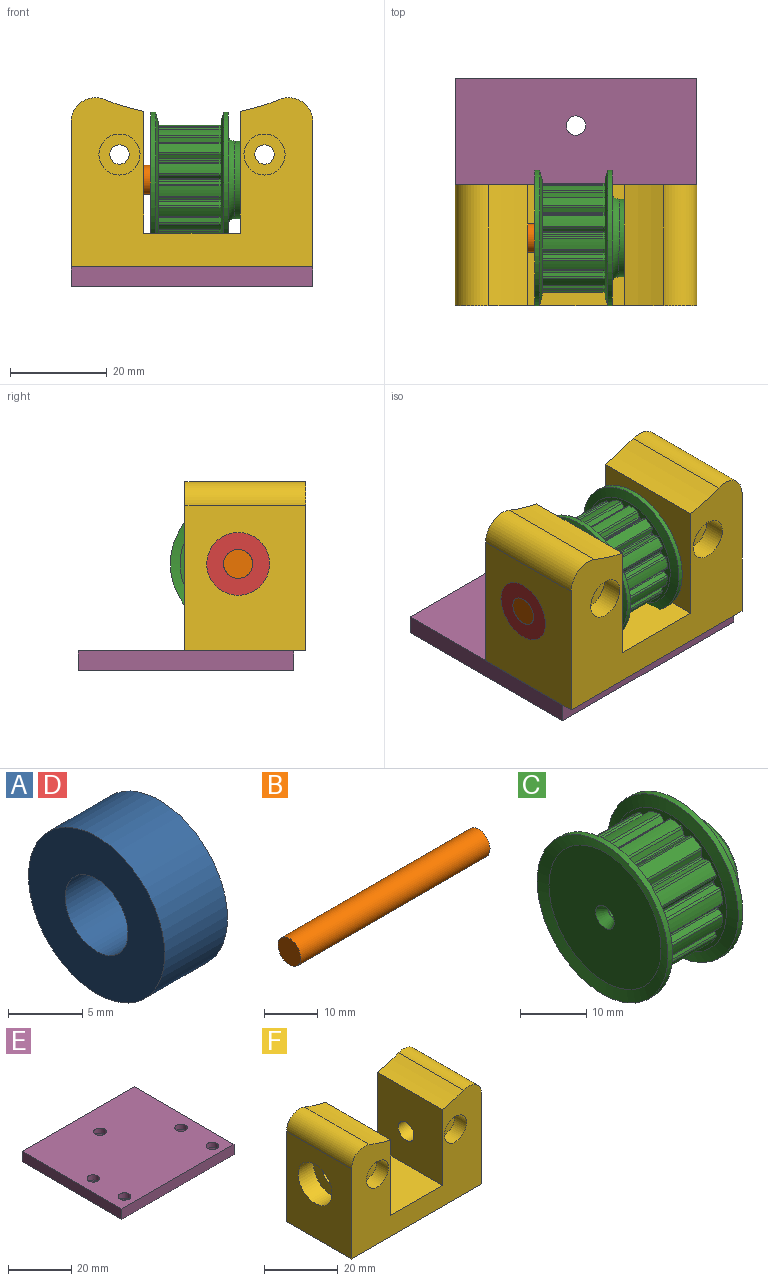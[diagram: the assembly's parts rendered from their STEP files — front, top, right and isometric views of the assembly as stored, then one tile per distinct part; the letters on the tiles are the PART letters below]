
ASSEMBLY  parts=6 mates=5
PART A: 4 faces, bbox 6x13x13 mm
  f0: cylinder r=3mm len=6mm, axis (1,0,0), area 113.1mm2, adj f2,f3
  f1: cylinder r=6.5mm len=13mm, axis (1,0,0), area 245mm2, adj f2,f3
  f2: plane 13x13mm, normal (-1,0,0), area 104.5mm2, adj f0,f1
  f3: plane 13x13mm, normal (1,0,0), area 104.5mm2, adj f0,f1
PART B: 3 faces, bbox 50x6x6 mm
  f0: cylinder r=3mm len=50mm, axis (1,0,0), area 942.5mm2, adj f1,f2
  f1: plane 6x6mm, normal (-1,0,0), area 28.3mm2, adj f0
  f2: plane 6x6mm, normal (1,0,0), area 28.3mm2, adj f0
PART C: 128 faces, bbox 21.5x28x28 mm
  f0: cone r=13mm half-angle=75deg, axis (-1,0,0), area 169.1mm2, adj f1,f27
  f1: cylinder r=14mm len=28mm, axis (1,0,0), area 88mm2, adj f0,f2
  f2: cone r=13mm half-angle=75deg, axis (-1,0,0), area 169.1mm2, adj f1,f126
  f3: cone r=13mm half-angle=75deg, axis (1,0,0), area 169.1mm2, adj f4,f36
  f4: cylinder r=14mm len=28mm, axis (-1,0,0), area 88mm2, adj f3,f5
  f5: cone r=13mm half-angle=75deg, axis (1,0,0), area 169.1mm2, adj f4,f127
  f6: cylinder r=8mm len=16mm, axis (1,0,0), area 179.9mm2, adj f7,f15,f17
  f7: cone r=7.75mm half-angle=45deg, axis (-1,0,0), area 34.4mm2, adj f6,f18
  f8: cone r=0.5mm half-angle=30deg, axis (-1,0,0), area 6.3mm2, adj f9
  f9: cylinder r=1mm len=2mm, axis (1,0,0), area 9.7mm2, adj f8,f10
  f10: cone r=1.5mm half-angle=30deg, axis (-1,0,0), area 18.8mm2, adj f9,f126
  f11: cone r=0.5mm half-angle=30deg, axis (1,0,0), area 4.2mm2, adj f12,f16
  f12: cylinder r=1mm len=2mm, axis (-1,0,0), area 9.7mm2, adj f11,f13
  f13: cone r=1.5mm half-angle=30deg, axis (1,0,0), area 18.8mm2, adj f12,f18
  f14: cylinder r=10mm len=20mm, axis (1,0,0), area 0.1mm2, adj f15,f127
  f15: torus R=10mm, axis (1,0,0), area 168.2mm2, adj f6,f14,f17
  f16: plane 1.15x1.15mm, normal (1,0,0), area 1mm2, adj f11
  f17: plane 15.97x8.73mm, normal (1,0,0), area 0.2mm2, adj f6,f15
  f18: plane 15x15mm, normal (1,0,0), area 164.1mm2, adj f7,f13
  f19: plane 13x0.77mm, normal (0,0.75,0.66), area 13.2mm2, adj f20,f25,f27,f36
  f20: cylinder r=0.6mm len=13mm, axis (1,0,0), area 5.5mm2, adj f19,f21,f27,f36
  f21: cylinder r=11.32mm len=13mm, axis (1,0,0), area 29.2mm2, adj f20,f22,f27,f36
  f22: cylinder r=0.6mm len=13mm, axis (1,0,0), area 5.5mm2, adj f21,f23,f27,f36
  f23: plane 13x1.02mm, normal (0,0.02,-1), area 13.2mm2, adj f22,f24,f27,f36
  f24: cylinder r=0.4mm len=13mm, axis (1,0,0), area 4.4mm2, adj f23,f27,f33,f36
  f25: cylinder r=0.4mm len=13mm, axis (1,0,0), area 4.4mm2, adj f19,f26,f27,f36
  f26: cylinder r=0.4mm len=13mm, axis (1,0,0), area 4.4mm2, adj f25,f27,f36,f125
  f27: plane 24x24mm, normal (1,0,0), area 73.5mm2, adj f0,f19,f20,f21,f22,f23,f24,f25
  f28: plane 13x0.94mm, normal (0,-0.39,-0.92), area 13.2mm2, adj f27,f29,f34,f36
  f29: cylinder r=0.6mm len=13mm, axis (1,0,0), area 5.5mm2, adj f27,f28,f30,f36
  f30: cylinder r=11.32mm len=13mm, axis (1,0,0), area 29.2mm2, adj f27,f29,f31,f36
  f31: cylinder r=0.6mm len=13mm, axis (1,0,0), area 5.5mm2, adj f27,f30,f32,f36
  f32: plane 13x0.97mm, normal (0,0.96,0.29), area 13.2mm2, adj f27,f31,f33,f36
  f33: cylinder r=0.4mm len=13mm, axis (1,0,0), area 4.4mm2, adj f24,f27,f32,f36
  f34: cylinder r=0.4mm len=13mm, axis (1,0,0), area 4.4mm2, adj f27,f28,f35,f36
  f35: cylinder r=0.4mm len=13mm, axis (1,0,0), area 4.4mm2, adj f27,f34,f36,f41
  f36: plane 24x24mm, normal (-1,0,0), area 73.5mm2, adj f3,f19,f20,f21,f22,f23,f24,f25
  f37: plane 13x0.74mm, normal (0,-0.73,-0.68), area 13.2mm2, adj f27,f36,f38,f42
  f38: cylinder r=0.6mm len=13mm, axis (1,0,0), area 5.5mm2, adj f27,f36,f37,f39
  f39: cylinder r=11.32mm len=13mm, axis (1,0,0), area 29.2mm2, adj f27,f36,f38,f40
  f40: cylinder r=0.6mm len=13mm, axis (1,0,0), area 5.5mm2, adj f27,f36,f39,f41
  f41: plane 13x1.01mm, normal (0,0.99,-0.12), area 13.2mm2, adj f27,f35,f36,f40
  f42: cylinder r=0.4mm len=13mm, axis (1,0,0), area 4.4mm2, adj f27,f36,f37,f43
  f43: cylinder r=0.4mm len=13mm, axis (1,0,0), area 4.4mm2, adj f27,f36,f42,f48
  f44: plane 13x0.96mm, normal (0,-0.95,-0.33), area 13.2mm2, adj f27,f36,f45,f49
  f45: cylinder r=0.6mm len=13mm, axis (1,0,0), area 5.5mm2, adj f27,f36,f44,f46
  f46: cylinder r=11.32mm len=13mm, axis (1,0,0), area 29.2mm2, adj f27,f36,f45,f47
  f47: cylinder r=0.6mm len=13mm, axis (1,0,0), area 5.5mm2, adj f27,f36,f46,f48
  f48: plane 13x0.87mm, normal (0,0.86,-0.52), area 13.2mm2, adj f27,f36,f43,f47
  f49: cylinder r=0.4mm len=13mm, axis (1,0,0), area 4.4mm2, adj f27,f36,f44,f50
  f50: cylinder r=0.4mm len=13mm, axis (1,0,0), area 4.4mm2, adj f27,f36,f49,f55
  f51: plane 13x1.01mm, normal (0,-1,0.09), area 13.2mm2, adj f27,f36,f52,f56
  f52: cylinder r=0.6mm len=13mm, axis (1,0,0), area 5.5mm2, adj f27,f36,f51,f53
  f53: cylinder r=11.32mm len=13mm, axis (1,0,0), area 29.2mm2, adj f27,f36,f52,f54
  f54: cylinder r=0.6mm len=13mm, axis (1,0,0), area 5.5mm2, adj f27,f36,f53,f55
  f55: plane 13x0.83mm, normal (0,0.57,-0.82), area 13.2mm2, adj f27,f36,f50,f54
  f56: cylinder r=0.4mm len=13mm, axis (1,0,0), area 4.4mm2, adj f27,f36,f51,f57
  f57: cylinder r=0.4mm len=13mm, axis (1,0,0), area 4.4mm2, adj f27,f36,f56,f62
  f58: plane 13x0.89mm, normal (0,-0.87,0.48), area 13.2mm2, adj f27,f36,f59,f63
  f59: cylinder r=0.6mm len=13mm, axis (1,0,0), area 5.5mm2, adj f27,f36,f58,f60
  f60: cylinder r=11.32mm len=13mm, axis (1,0,0), area 29.2mm2, adj f27,f36,f59,f61
  f61: cylinder r=0.6mm len=13mm, axis (1,0,0), area 5.5mm2, adj f27,f36,f60,f62
  f62: plane 13x1mm, normal (0,0.19,-0.98), area 13.2mm2, adj f27,f36,f57,f61
  f63: cylinder r=0.4mm len=13mm, axis (1,0,0), area 4.4mm2, adj f27,f36,f58,f64
  f64: cylinder r=0.4mm len=13mm, axis (1,0,0), area 4.4mm2, adj f27,f36,f63,f69
  f65: plane 13x0.81mm, normal (0,-0.6,0.8), area 13.2mm2, adj f27,f36,f66,f70
  f66: cylinder r=0.6mm len=13mm, axis (1,0,0), area 5.5mm2, adj f27,f36,f65,f67
  f67: cylinder r=11.32mm len=13mm, axis (1,0,0), area 29.2mm2, adj f27,f36,f66,f68
  f68: cylinder r=0.6mm len=13mm, axis (1,0,0), area 5.5mm2, adj f27,f36,f67,f69
  f69: plane 13x0.99mm, normal (0,-0.22,-0.97), area 13.2mm2, adj f27,f36,f64,f68
  f70: cylinder r=0.4mm len=13mm, axis (1,0,0), area 4.4mm2, adj f27,f36,f65,f71
  f71: cylinder r=0.4mm len=13mm, axis (1,0,0), area 4.4mm2, adj f27,f36,f70,f76
  f72: plane 13x0.99mm, normal (0,-0.22,0.97), area 13.2mm2, adj f27,f36,f73,f77
  f73: cylinder r=0.6mm len=13mm, axis (1,0,0), area 5.5mm2, adj f27,f36,f72,f74
  f74: cylinder r=11.32mm len=13mm, axis (1,0,0), area 29.2mm2, adj f27,f36,f73,f75
  f75: cylinder r=0.6mm len=13mm, axis (1,0,0), area 5.5mm2, adj f27,f36,f74,f76
  f76: plane 13x0.81mm, normal (0,-0.6,-0.8), area 13.2mm2, adj f27,f36,f71,f75
  f77: cylinder r=0.4mm len=13mm, axis (1,0,0), area 4.4mm2, adj f27,f36,f72,f78
  f78: cylinder r=0.4mm len=13mm, axis (1,0,0), area 4.4mm2, adj f27,f36,f77,f83
  f79: plane 13x1mm, normal (0,0.19,0.98), area 13.2mm2, adj f27,f36,f80,f84
  f80: cylinder r=0.6mm len=13mm, axis (1,0,0), area 5.5mm2, adj f27,f36,f79,f81
  f81: cylinder r=11.32mm len=13mm, axis (1,0,0), area 29.2mm2, adj f27,f36,f80,f82
  f82: cylinder r=0.6mm len=13mm, axis (1,0,0), area 5.5mm2, adj f27,f36,f81,f83
  f83: plane 13x0.89mm, normal (0,-0.87,-0.48), area 13.2mm2, adj f27,f36,f78,f82
  f84: cylinder r=0.4mm len=13mm, axis (1,0,0), area 4.4mm2, adj f27,f36,f79,f85
  f85: cylinder r=0.4mm len=13mm, axis (1,0,0), area 4.4mm2, adj f27,f36,f84,f90
  f86: plane 13x0.83mm, normal (0,0.57,0.82), area 13.2mm2, adj f27,f36,f87,f91
  f87: cylinder r=0.6mm len=13mm, axis (1,0,0), area 5.5mm2, adj f27,f36,f86,f88
  f88: cylinder r=11.32mm len=13mm, axis (1,0,0), area 29.2mm2, adj f27,f36,f87,f89
  f89: cylinder r=0.6mm len=13mm, axis (1,0,0), area 5.5mm2, adj f27,f36,f88,f90
  f90: plane 13x1.01mm, normal (0,-1,-0.09), area 13.2mm2, adj f27,f36,f85,f89
  f91: cylinder r=0.4mm len=13mm, axis (1,0,0), area 4.4mm2, adj f27,f36,f86,f92
  f92: cylinder r=0.4mm len=13mm, axis (1,0,0), area 4.4mm2, adj f27,f36,f91,f97
  f93: plane 13x0.87mm, normal (0,0.86,0.52), area 13.2mm2, adj f27,f36,f94,f98
  f94: cylinder r=0.6mm len=13mm, axis (1,0,0), area 5.5mm2, adj f27,f36,f93,f95
  f95: cylinder r=11.32mm len=13mm, axis (1,0,0), area 29.2mm2, adj f27,f36,f94,f96
  f96: cylinder r=0.6mm len=13mm, axis (1,0,0), area 5.5mm2, adj f27,f36,f95,f97
  f97: plane 13x0.96mm, normal (0,-0.95,0.33), area 13.2mm2, adj f27,f36,f92,f96
  f98: cylinder r=0.4mm len=13mm, axis (1,0,0), area 4.4mm2, adj f27,f36,f93,f99
  f99: cylinder r=0.4mm len=13mm, axis (1,0,0), area 4.4mm2, adj f27,f36,f98,f104
  f100: plane 13x1.01mm, normal (0,0.99,0.12), area 13.2mm2, adj f27,f36,f101,f105
  f101: cylinder r=0.6mm len=13mm, axis (1,0,0), area 5.5mm2, adj f27,f36,f100,f102
  f102: cylinder r=11.32mm len=13mm, axis (1,0,0), area 29.2mm2, adj f27,f36,f101,f103
  f103: cylinder r=0.6mm len=13mm, axis (1,0,0), area 5.5mm2, adj f27,f36,f102,f104
  f104: plane 13x0.74mm, normal (0,-0.73,0.68), area 13.2mm2, adj f27,f36,f99,f103
  f105: cylinder r=0.4mm len=13mm, axis (1,0,0), area 4.4mm2, adj f27,f36,f100,f106
  f106: cylinder r=0.4mm len=13mm, axis (1,0,0), area 4.4mm2, adj f27,f36,f105,f111
  f107: plane 13x0.97mm, normal (0,0.96,-0.29), area 13.2mm2, adj f27,f36,f108,f112
  f108: cylinder r=0.6mm len=13mm, axis (1,0,0), area 5.5mm2, adj f27,f36,f107,f109
  f109: cylinder r=11.32mm len=13mm, axis (1,0,0), area 29.2mm2, adj f27,f36,f108,f110
  f110: cylinder r=0.6mm len=13mm, axis (1,0,0), area 5.5mm2, adj f27,f36,f109,f111
  f111: plane 13x0.94mm, normal (0,-0.39,0.92), area 13.2mm2, adj f27,f36,f106,f110
  f112: cylinder r=0.4mm len=13mm, axis (1,0,0), area 4.4mm2, adj f27,f36,f107,f113
  f113: cylinder r=0.4mm len=13mm, axis (1,0,0), area 4.4mm2, adj f27,f36,f112,f117
  f114: cylinder r=0.4mm len=13mm, axis (1,0,0), area 4.4mm2, adj f27,f36,f119,f122
  f115: cylinder r=11.32mm len=13mm, axis (1,0,0), area 29.2mm2, adj f27,f36,f116,f118
  f116: cylinder r=0.6mm len=13mm, axis (1,0,0), area 5.5mm2, adj f27,f36,f115,f119
  f117: plane 13x1.02mm, normal (0,0.02,1), area 13.2mm2, adj f27,f36,f113,f118
  f118: cylinder r=0.6mm len=13mm, axis (1,0,0), area 5.5mm2, adj f27,f36,f115,f117
  f119: plane 13x0.77mm, normal (0,0.75,-0.66), area 13.2mm2, adj f27,f36,f114,f116
  f120: cylinder r=11.32mm len=13mm, axis (1,0,0), area 29.2mm2, adj f27,f36,f121,f124
  f121: cylinder r=0.6mm len=13mm, axis (1,0,0), area 5.5mm2, adj f27,f36,f120,f125
  f122: cylinder r=0.4mm len=13mm, axis (1,0,0), area 4.4mm2, adj f27,f36,f114,f123
  f123: plane 13x0.92mm, normal (0,0.42,0.91), area 13.2mm2, adj f27,f36,f122,f124
  f124: cylinder r=0.6mm len=13mm, axis (1,0,0), area 5.5mm2, adj f27,f36,f120,f123
  f125: plane 13x0.92mm, normal (0,0.42,-0.91), area 13.2mm2, adj f26,f27,f36,f121
  f126: plane 24x24mm, normal (-1,0,0), area 439.8mm2, adj f2,f10
  f127: plane 24x24mm, normal (1,0,0), area 138.2mm2, adj f5,f14
PART D: same geometry as A
PART E: 16 faces, bbox 50x44.6x4 mm
  f0: plane 50x4mm, normal (0,-1,0), area 200mm2, adj f1,f7,f9,f10
  f1: plane 44.62x4mm, normal (-1,0,0), area 178.5mm2, adj f0,f2,f9,f10
  f2: plane 50x4mm, normal (0,1,0), area 200mm2, adj f1,f7,f9,f10
  f3: cylinder r=2mm len=4mm, axis (0,0,1), area 25.1mm2, adj f10,f13
  f4: cylinder r=2mm len=4mm, axis (0,0,1), area 25.1mm2, adj f10,f12
  f5: cylinder r=2mm len=4mm, axis (0,0,1), area 25.1mm2, adj f10,f15
  f6: cylinder r=2mm len=4mm, axis (0,0,1), area 25.1mm2, adj f10,f14
  f7: plane 44.62x4mm, normal (1,0,0), area 178.5mm2, adj f0,f2,f9,f10
  f8: cylinder r=2mm len=4mm, axis (0,0,1), area 25.1mm2, adj f10,f11
  f9: plane 50x44.62mm, normal (0,0,-1), area 1979.5mm2, adj f0,f1,f2,f7,f11,f12,f13,f14
  f10: plane 50x44.62mm, normal (0,0,1), area 2168mm2, adj f0,f1,f2,f3,f4,f5,f6,f7
  f11: cone r=2mm half-angle=45deg, axis (0,0,-1), area 53.3mm2, adj f8,f9
  f12: cone r=2mm half-angle=45deg, axis (0,0,-1), area 53.3mm2, adj f4,f9
  f13: cone r=2mm half-angle=45deg, axis (0,0,-1), area 53.3mm2, adj f3,f9
  f14: cone r=2mm half-angle=45deg, axis (0,0,-1), area 53.3mm2, adj f6,f9
  f15: cone r=2mm half-angle=45deg, axis (0,0,-1), area 53.3mm2, adj f5,f9
PART F: 28 faces, bbox 50x25x35 mm
  f0: cylinder r=2mm len=20.5mm, axis (0,1,0), area 257.6mm2, adj f14,f21
  f1: cylinder r=2mm len=20.5mm, axis (0,1,0), area 257.6mm2, adj f14,f23
  f2: cylinder r=3mm len=9mm, axis (1,0,0), area 169.6mm2, adj f3,f19
  f3: plane 25.16x25mm, normal (1,0,0), area 600.8mm2, adj f2,f4,f12,f13,f14
  f4: cylinder r=48.49mm len=25mm, axis (0,1,0), area 212.7mm2, adj f3,f5,f13,f14
  f5: cylinder r=5mm len=25mm, axis (0,1,0), area 244.3mm2, adj f4,f6,f13,f14
  f6: plane 30x25mm, normal (-1,0,0), area 617.3mm2, adj f5,f7,f13,f14,f18
  f7: plane 50x25mm, normal (0,0,-1), area 1224.9mm2, adj f6,f8,f13,f14,f24,f26
  f8: plane 30x25mm, normal (1,0,0), area 617.3mm2, adj f7,f9,f13,f14,f15
  f9: cylinder r=5mm len=25mm, axis (0,1,0), area 244.3mm2, adj f8,f10,f13,f14
  f10: cylinder r=48.49mm len=25mm, axis (0,1,0), area 212.7mm2, adj f9,f11,f13,f14
  f11: plane 25.16x25mm, normal (-1,0,0), area 600.8mm2, adj f10,f12,f13,f14,f17
  f12: plane 25x20mm, normal (0,0,1), area 500mm2, adj f3,f11,f13,f14
  f13: plane 50x35mm, normal (0,-1,0), area 1037.2mm2, adj f3,f4,f5,f6,f7,f8,f9,f10
  f14: plane 50x35mm, normal (0,1,0), area 1125.6mm2, adj f0,f1,f3,f4,f5,f6,f7,f8
  f15: cylinder r=6.5mm len=13mm, axis (1,0,0), area 245mm2, adj f8,f16
  f16: plane 13x13mm, normal (1,0,0), area 104.5mm2, adj f15,f17
  f17: cylinder r=3mm len=9mm, axis (1,0,0), area 169.6mm2, adj f11,f16
  f18: cylinder r=6.5mm len=13mm, axis (-1,0,0), area 245mm2, adj f6,f19
  f19: plane 13x13mm, normal (-1,0,0), area 104.5mm2, adj f2,f18
  f20: cylinder r=4.25mm len=8.5mm, axis (0,-1,0), area 120.2mm2, adj f13,f21
  f21: plane 8.5x8.5mm, normal (0,-1,0), area 44.2mm2, adj f0,f20
  f22: cylinder r=4.25mm len=8.5mm, axis (0,-1,0), area 120.2mm2, adj f13,f23
  f23: plane 8.5x8.5mm, normal (0,-1,0), area 44.2mm2, adj f1,f22
  f24: cylinder r=2mm len=8mm, axis (0,0,-1), area 100.5mm2, adj f7,f25
  f25: plane 4x4mm, normal (0,0,-1), area 12.6mm2, adj f24
  f26: cylinder r=2mm len=8mm, axis (0,0,-1), area 100.5mm2, adj f7,f27
  f27: plane 4x4mm, normal (0,0,-1), area 12.6mm2, adj f26
PLACE A rot(axis=(0,1,0),180deg) t=(65.36,131.51,-180.68)mm
PLACE B t=(21.36,155.22,-216.68)mm
PLACE C t=(13.36,78.66,-198.68)mm
PLACE D rot(axis=(0,-1,0),180deg) t=(21.36,131.51,-180.68)mm
PLACE E t=(21.36,89.66,-216.68)mm
PLACE F t=(21.36,89.66,-216.68)mm
MATE fastened A.f0 <-> F.f15  axis (-1,0,0) through (40.36,78.66,-198.68)mm
MATE fastened D.f0 <-> F.f18  axis (1,0,0) through (2.36,78.66,-198.68)mm
MATE fastened C.f4 <-> B.f0  axis (1,0,0) through (34.36,78.66,-198.68)mm
MATE fastened E.f6 <-> F.f24  axis (0,0,1) through (40.94,85.34,-216.68)mm
MATE revolute B.f0 <-> A.f0  axis (1,0,0) through (46.36,78.66,-198.68)mm
